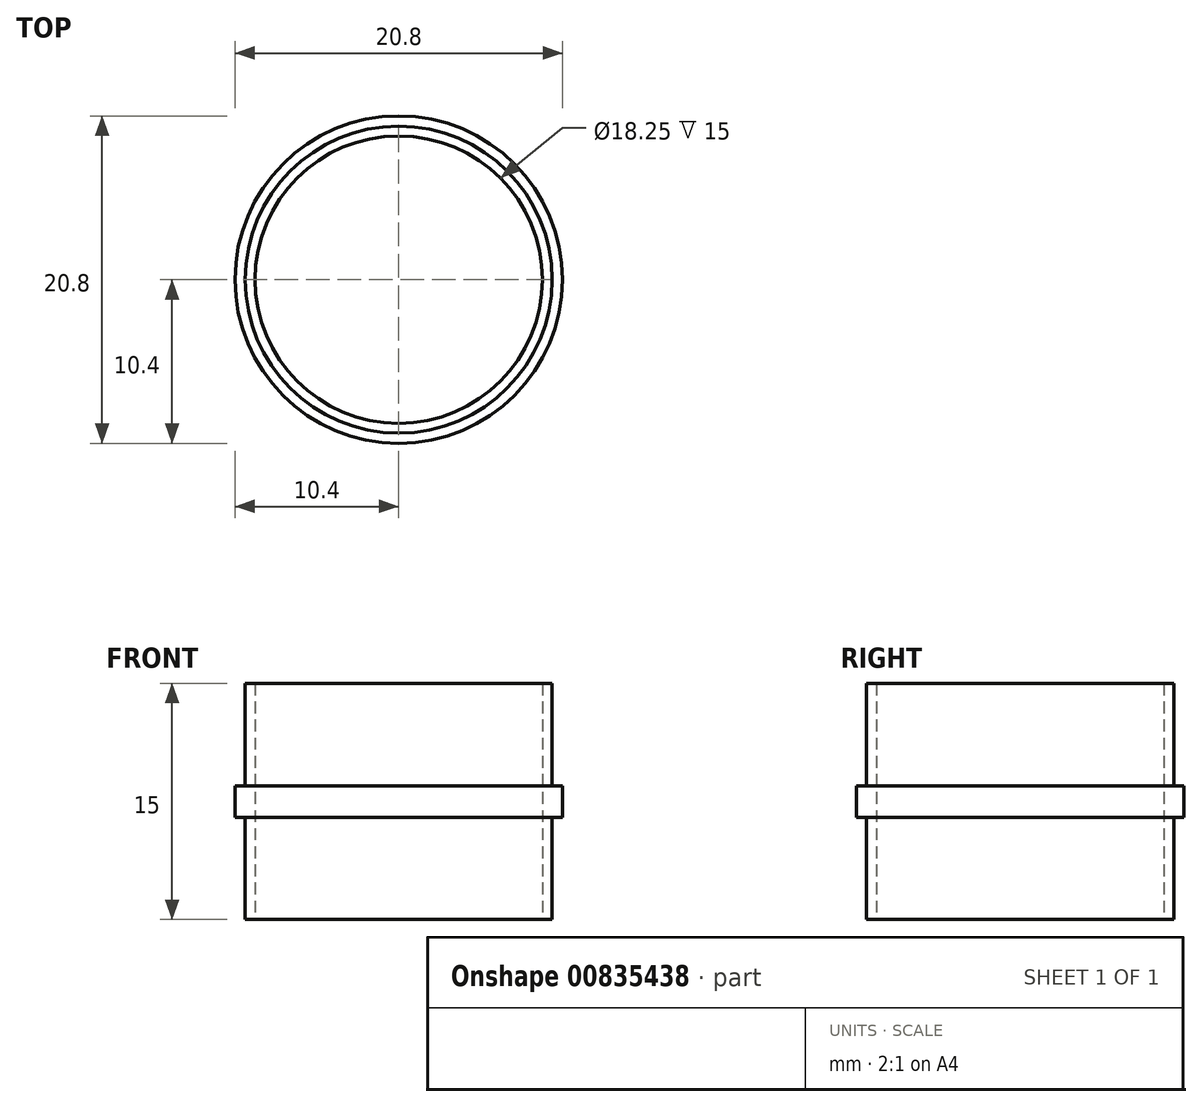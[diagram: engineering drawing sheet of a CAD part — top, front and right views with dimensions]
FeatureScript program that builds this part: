
annotation { "Feature Type Name" : "Feature", "Feature Type Description" : "" }
export const myFeature = defineFeature(function(context is Context, id is Id, definition is map)
    precondition{}
    {
        {
            var Q0;
            Q0=qCreatedBy(makeId("Top.planeOp"),FACE);
            var sketch = newSketch(context, id + "F0", { "sketchPlane" : qUnion([Q0])});
            skCircle(sketch, "E0", {"center": v(0, 0) * mm, "radius": 9.75 * mm});
            skCircle(sketch, "E1", {"center": v(0, 0) * mm, "radius": 9.12 * mm});
            skSolve(sketch);
        }
        {
            var Q0;
            Q0 = qSketchRegion(id + "F0", true);
            extrude(context, id + "F1", {"entities" : qUnion([Q0]), "endBound" : BoundingType.SYMMETRIC, "depth" : 15 * mm, "offsetDistance" : 25 * mm});
        }
        {
            var Q0;
            Q0=qCreatedBy(makeId("Top.planeOp"),FACE);
            var sketch = newSketch(context, id + "F2", { "sketchPlane" : qUnion([Q0])});
            skCircle(sketch, "E2", {"center": v(0, 0) * mm, "radius": 10.4 * mm});
            skCircle(sketch, "E3", {"center": v(0, 0) * mm, "radius": 9.75 * mm});
            skSolve(sketch);
        }
        {
            var Q0;
            Q0 = qSketchRegion(id + "F2", true);
            extrude(context, id + "F3", {"entities" : qUnion([Q0]), "operationType" : NewBodyOperationType.ADD, "endBound" : BoundingType.SYMMETRIC, "depth" : 2 * mm, "offsetDistance" : 25 * mm});
        }
    });
